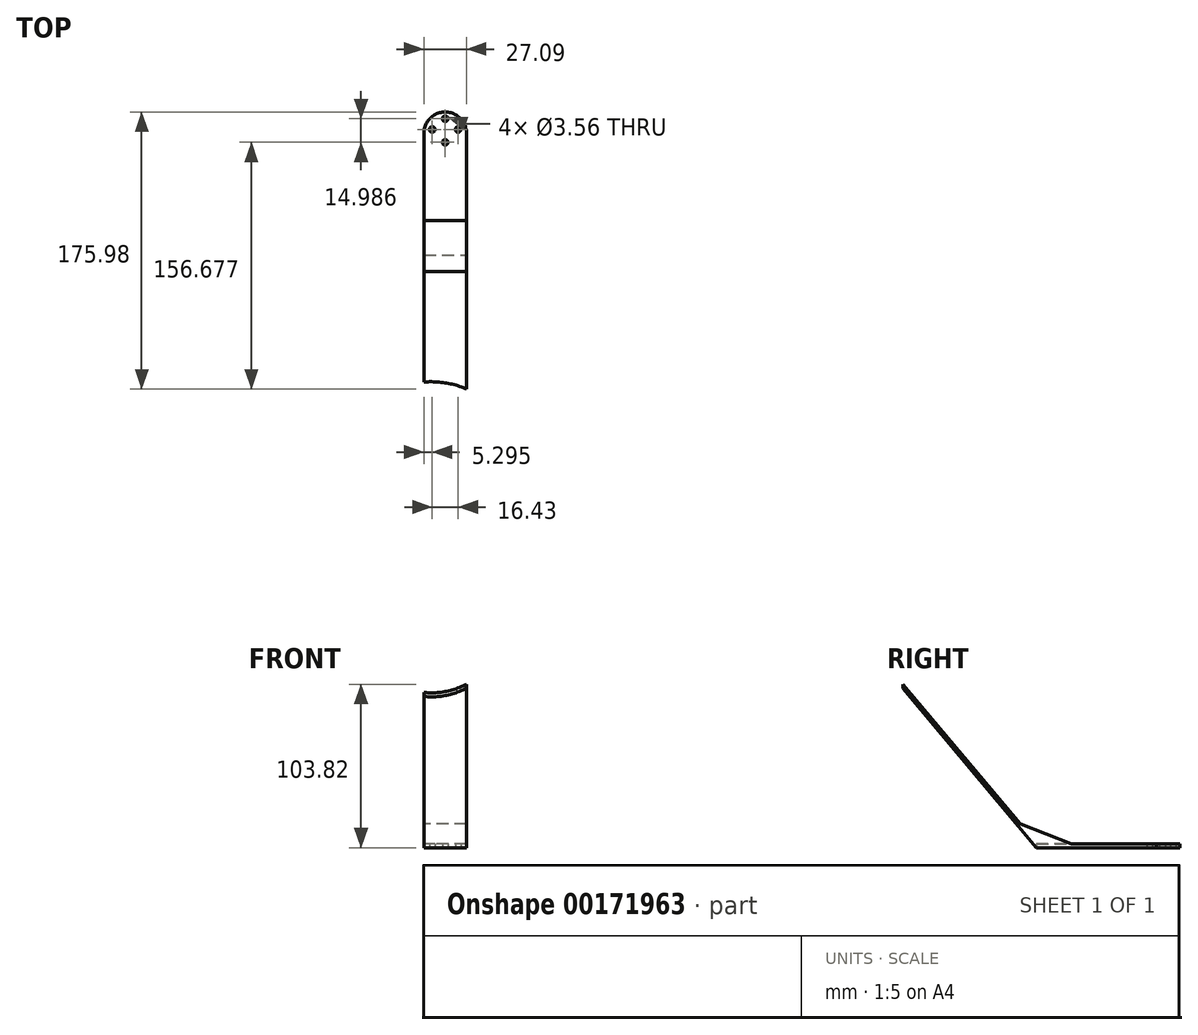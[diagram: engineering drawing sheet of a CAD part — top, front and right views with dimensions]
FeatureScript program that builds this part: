
annotation { "Feature Type Name" : "Feature", "Feature Type Description" : "" }
export const myFeature = defineFeature(function(context is Context, id is Id, definition is map)
    precondition{}
    {
        {
            var Q0;
            Q0=qCreatedBy(makeId("Top.planeOp"),FACE);
            var sketch = newSketch(context, id + "F0", { "sketchPlane" : qUnion([Q0])});
            skCircle(sketch, "E0", {"center": v(0, 38.91) * mm, "radius": 13.5 * mm});
            skSolve(sketch);
        }
        {
            var Q0;
            Q0=makeQuery(id+"F0.imprint","IMPRINT",FACE,{"disambiguationData":[TD([[makeQuery(id+"F0.imprint","IMPRINT",EDGE,{"derivedFrom":sQuery(id+"F0.wireOp",EDGE,"E0")}),1.0]])]});
            extrude(context, id + "F1", {"entities" : qUnion([Q0]), "depth" : 2.54 * mm});
        }
        {
            var Q0;
            Q0=qCreatedBy(makeId("Top.planeOp"),FACE);
            var sketch = newSketch(context, id + "F2", { "sketchPlane" : qUnion([Q0])});
            skLineSegment(sketch, "E1.bottom", {"start": v(-13.44, 37.63) * mm, "end": v(13.58, 37.63) * mm});
            skLineSegment(sketch, "E1.top", {"start": v(-13.44, -38.57) * mm, "end": v(13.58, -38.57) * mm});
            skLineSegment(sketch, "E1.left", {"start": v(-13.44, 37.63) * mm, "end": v(-13.44, -38.57) * mm});
            skLineSegment(sketch, "E1.right", {"start": v(13.58, 37.63) * mm, "end": v(13.58, -38.57) * mm});
            skSolve(sketch);
        }
        {
            var Q0;
            Q0 = qSketchRegion(id + "F2", true);
            extrude(context, id + "F3", {"entities" : qUnion([Q0]), "operationType" : NewBodyOperationType.ADD, "depth" : 2.54 * mm});
        }
        {
            var Q0;
            Q0=qCreatedBy(makeId("Top.planeOp"),FACE);
            var sketch = newSketch(context, id + "F4", { "sketchPlane" : qUnion([Q0])});
            skCircle(sketch, "E2", {"center": v(-8.21, 41.3) * mm, "radius": 1.78 * mm});
            skCircle(sketch, "E3", {"center": v(0, 48.1) * mm, "radius": 1.78 * mm});
            skCircle(sketch, "E4", {"center": v(0, 33.12) * mm, "radius": 1.78 * mm});
            skCircle(sketch, "E5.MirrorC", {"center": v(8.21, 41.3) * mm, "radius": 1.78 * mm});
            skSolve(sketch);
        }
        {
            var Q0;
            Q0 = qSketchRegion(id + "F4", true);
            var Q1;
            Q1 = qSketchRegion(id + "F6", true);
            extrude(context, id + "F5", {"entities" : qUnion([Q0, Q1]), "operationType" : NewBodyOperationType.REMOVE, "endBound" : BoundingType.THROUGH_ALL, "depth" : 2.54 * mm});
        }
        {
            var Q0;
            Q0=makeQuery(id+"F3.opExtrude","SWEPT_FACE",FACE,{"disambiguationData":[OSD([sQuery(id+"F2.wireOp",EDGE,"E1.right")])]});
            var sketch = newSketch(context, id + "F6", { "sketchPlane" : qUnion([Q0])});
            skLineSegment(sketch, "E6", {"start": v(-38.57, 0) * mm, "end": v(-136.53, 116.75) * mm});
            skLineSegment(sketch, "E7", {"start": v(-38.57, 2.54) * mm, "end": v(-134.4, 116.75) * mm});
            skLineSegment(sketch, "E8", {"start": v(-134.4, 116.75) * mm, "end": v(-136.53, 116.75) * mm});
            skLineSegment(sketch, "E9", {"start": v(-38.57, 2.54) * mm, "end": v(-38.57, 0) * mm});
            skSolve(sketch);
        }
        {
            var Q0;
            Q0=makeQuery(id+"F6.imprint","IMPRINT",FACE,{"disambiguationData":[TD([[makeQuery(id+"F6.imprint","IMPRINT",EDGE,{"derivedFrom":sQuery(id+"F6.wireOp",EDGE,"E6")}),-1.0]])]});
            extrude(context, id + "F7", {"entities" : qUnion([Q0]), "operationType" : NewBodyOperationType.ADD, "oppositeDirection" : true, "depth" : 26.99 * mm});
        }
        {
            var Q0;
            Q0=makeQuery(id+"F7.opExtrude","CAP_FACE",FACE,{"disambiguationData":[OSD([sQuery(id+"F6.wireOp",EDGE,"E6"),sQuery(id+"F6.wireOp",EDGE,"E7"),sQuery(id+"F6.wireOp",EDGE,"E8"),sQuery(id+"F6.wireOp",EDGE,"E9")])],"isStart":false});
            var sketch = newSketch(context, id + "F8", { "sketchPlane" : qUnion([Q0])});
            skLineSegment(sketch, "E10", {"start": v(49, 14.97) * mm, "end": v(16.43, 2.54) * mm});
            skLineSegment(sketch, "E11", {"start": v(49, 14.97) * mm, "end": v(38.57, 2.54) * mm});
            skLineSegment(sketch, "E12", {"start": v(38.57, 2.54) * mm, "end": v(16.43, 2.54) * mm});
            skSolve(sketch);
        }
        {
            var Q0;
            Q0=makeQuery(id+"F8.imprint","IMPRINT",FACE,{"disambiguationData":[TD([[makeQuery(id+"F8.imprint","IMPRINT",EDGE,{"derivedFrom":sQuery(id+"F8.wireOp",EDGE,"E10")}),1.0]])]});
            extrude(context, id + "F9", {"entities" : qUnion([Q0]), "operationType" : NewBodyOperationType.ADD, "oppositeDirection" : true, "depth" : 26.99 * mm});
        }
        {
            var Q0;
            Q0=makeQuery(id+"F7.opExtrude","SWEPT_FACE",FACE,{"disambiguationData":[OSD([sQuery(id+"F6.wireOp",EDGE,"E8")])]});
            var sketch = newSketch(context, id + "F10", { "sketchPlane" : qUnion([Q0])});
            skCircle(sketch, "E13", {"center": v(0, -175.38) * mm, "radius": 60.96 * mm});
            skSolve(sketch);
        }
        {
            var Q0;
            Q0=makeQuery(id+"F10.imprint","IMPRINT",FACE,{"disambiguationData":[TD([[makeQuery(id+"F10.imprint","IMPRINT",EDGE,{"derivedFrom":sQuery(id+"F10.wireOp",EDGE,"E13")}),1.0]])]});
            extrude(context, id + "F11", {"entities" : qUnion([Q0]), "oppositeDirection" : true, "depth" : 50.8 * mm});
        }
        {
            var Q0;
            Q0=makeQuery(id+"F11.opExtrude","CAP_FACE",FACE,{"disambiguationData":[OSD([sQuery(id+"F6.wireOp",EDGE,"E6"),sQuery(id+"F6.wireOp",EDGE,"E7"),sQuery(id+"F6.wireOp",EDGE,"E8"),sQuery(id+"F10.wireOp",EDGE,"E13")])],"isStart":true});
            var sketch = newSketch(context, id + "F12", { "sketchPlane" : qUnion([Q0])});
            skCircle(sketch, "E14", {"center": v(-8.77, -175.5) * mm, "radius": 56.55 * mm});
            skSolve(sketch);
        }
        {
            var Q0;
            Q0 = qSketchRegion(id + "F12", true);
            extrude(context, id + "F13", {"entities" : qUnion([Q0]), "operationType" : NewBodyOperationType.REMOVE, "endBound" : BoundingType.THROUGH_ALL, "oppositeDirection" : true, "depth" : 50.8 * mm});
        }
        {
            var Q0;
            Q0=makeQuery(id+"F11.opExtrude","CAP_FACE",FACE,{"disambiguationData":[OSD([sQuery(id+"F6.wireOp",EDGE,"E6"),sQuery(id+"F6.wireOp",EDGE,"E7"),sQuery(id+"F6.wireOp",EDGE,"E8"),sQuery(id+"F10.wireOp",EDGE,"E13")])],"isStart":false});
            var sketch = newSketch(context, id + "F14", { "sketchPlane" : qUnion([Q0])});
            skLineSegment(sketch, "E15", {"start": v(0, 236.34) * mm, "end": v(0, 231.36) * mm});
            skLineSegment(sketch, "E16", {"start": v(-18.45, 119.79) * mm, "end": v(-18.45, 117.28) * mm});
            skSolve(sketch);
        }
        {
            var Q0;
            Q0 = qSketchRegion(id + "F14", true);
            var Q1;
            {var subQ0=sQuery(id+"F14.wireOp",EDGE,"E16");Q1=makeQuery(id+"F14.imprint","IMPRINT",FACE,{"disambiguationData":[TD([[makeQuery(id+"F14.imprint","IMPRINT",EDGE,{"derivedFrom":subQ0}),-1.0]])]});}
            extrude(context, id + "F15", {"entities" : qUnion([Q0, Q1]), "operationType" : NewBodyOperationType.REMOVE, "endBound" : BoundingType.THROUGH_ALL, "oppositeDirection" : true, "depth" : 50.8 * mm});
        }
        {
            var Q0;
            Q0=makeQuery(id+"F11.opExtrude","CAP_FACE",FACE,{"disambiguationData":[OSD([sQuery(id+"F6.wireOp",EDGE,"E6"),sQuery(id+"F6.wireOp",EDGE,"E7"),sQuery(id+"F6.wireOp",EDGE,"E8"),sQuery(id+"F10.wireOp",EDGE,"E13")])],"isStart":false});
            var sketch = newSketch(context, id + "F16", { "sketchPlane" : qUnion([Q0])});
            skLineSegment(sketch, "E17", {"start": v(-12.94, 234.95) * mm, "end": v(-12.94, 231.89) * mm});
            skSolve(sketch);
        }
        {
            var Q0;
            Q0 = qSketchRegion(id + "F16", true);
            var Q1;
            {var subQ0=sQuery(id+"F16.wireOp",EDGE,"E17");Q1=makeQuery(id+"F16.imprint","IMPRINT",FACE,{"disambiguationData":[TD([[makeQuery(id+"F16.imprint","IMPRINT",EDGE,{"derivedFrom":subQ0}),-1.0]])]});}
            extrude(context, id + "F17", {"entities" : qUnion([Q0, Q1]), "operationType" : NewBodyOperationType.REMOVE, "oppositeDirection" : true, "depth" : 50.8 * mm});
        }
        {
            var Q0;
            Q0=makeQuery(id+"F9.boolean.opBoolean","MERGE",FACE,{"derivedFrom":[makeQuery(id+"F7.opExtrude","CAP_FACE",FACE,{"disambiguationData":[OSD([sQuery(id+"F6.wireOp",EDGE,"E6"),sQuery(id+"F6.wireOp",EDGE,"E7"),sQuery(id+"F6.wireOp",EDGE,"E8"),sQuery(id+"F6.wireOp",EDGE,"E9")])],"isStart":false}),makeQuery(id+"F9.opExtrude","CAP_FACE",FACE,{"disambiguationData":[OSD([sQuery(id+"F8.wireOp",EDGE,"E10"),sQuery(id+"F8.wireOp",EDGE,"E11"),sQuery(id+"F8.wireOp",EDGE,"E12")])],"isStart":true})]});
            var sketch = newSketch(context, id + "F18", { "sketchPlane" : qUnion([Q0])});
            skLineSegment(sketch, "E18", {"start": v(105.32, 79.55) * mm, "end": v(117.28, 79.55) * mm});
            skLineSegment(sketch, "E19", {"start": v(105.32, 79.55) * mm, "end": v(116.02, 92.3) * mm});
            skLineSegment(sketch, "E20", {"start": v(116.02, 92.3) * mm, "end": v(117.28, 79.55) * mm});
            skSolve(sketch);
        }
        {
            var Q0;
            Q0 = qSketchRegion(id + "F18", true);
            extrude(context, id + "F19", {"entities" : qUnion([Q0]), "depth" : 25.4 * mm});
        }
        {
            var Q0;
            Q0 = qSketchRegion(id + "F18", true);
            extrude(context, id + "F20", {"entities" : qUnion([Q0]), "oppositeDirection" : true, "depth" : 26.99 * mm});
        }
        {
            var Q0;
            Q0=makeQuery(id+"F19.opExtrude","CAP_FACE",FACE,{"disambiguationData":[OSD([sQuery(id+"F18.wireOp",EDGE,"E18"),sQuery(id+"F18.wireOp",EDGE,"E19"),sQuery(id+"F18.wireOp",EDGE,"E20")])],"isStart":false});
            extrude(context, id + "F21", {"entities" : qUnion([Q0]), "operationType" : NewBodyOperationType.REMOVE, "oppositeDirection" : true, "depth" : 25.4 * mm});
        }
        {
            var Q0;
            Q0=makeQuery(id+"F11.opExtrude","SWEPT_BODY",BODY,{"disambiguationData":[OSD([sQuery(id+"F6.wireOp",EDGE,"E6"),sQuery(id+"F6.wireOp",EDGE,"E7"),sQuery(id+"F6.wireOp",EDGE,"E8"),sQuery(id+"F10.wireOp",EDGE,"E13")])]});
            deleteBodies(context, id + "F22", {"entities" : qUnion([Q0])});
        }
        {
            var Q0;
            Q0=makeQuery(id+"F20.opExtrude","SWEPT_BODY",BODY,{"disambiguationData":[OSD([sQuery(id+"F18.wireOp",EDGE,"E18"),sQuery(id+"F18.wireOp",EDGE,"E19"),sQuery(id+"F18.wireOp",EDGE,"E20")])]});
            deleteBodies(context, id + "F23", {"entities" : qUnion([Q0])});
        }
    });
